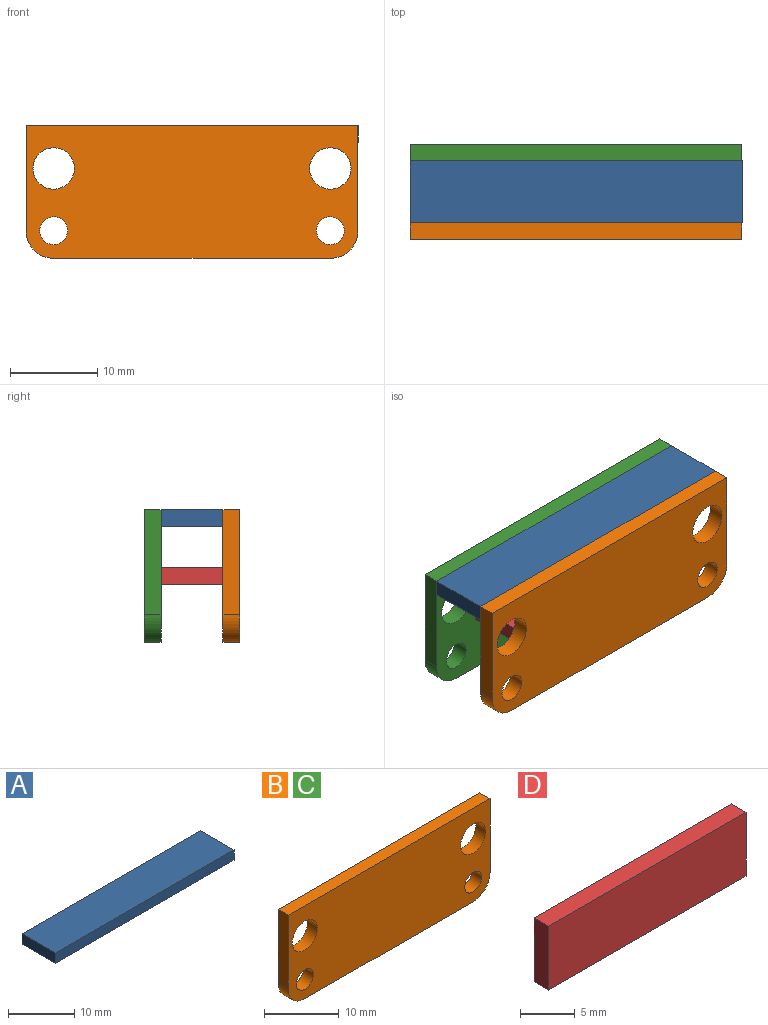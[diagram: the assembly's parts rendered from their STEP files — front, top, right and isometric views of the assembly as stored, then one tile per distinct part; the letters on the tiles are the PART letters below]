
ASSEMBLY  parts=4 mates=3
PART A: 6 faces, bbox 38.1x7.1x1.9 mm
  f0: plane 7.11x1.9mm, normal (-1,0,0), area 13.5mm2, adj f1,f3,f4,f5
  f1: plane 38.1x1.9mm, normal (0,-1,0), area 72.3mm2, adj f0,f2,f4,f5
  f2: plane 7.11x1.9mm, normal (1,0,0), area 13.5mm2, adj f1,f3,f4,f5
  f3: plane 38.1x1.9mm, normal (0,1,0), area 72.3mm2, adj f0,f2,f4,f5
  f4: plane 38.1x7.11mm, normal (0,0,1), area 271mm2, adj f0,f1,f2,f3
  f5: plane 38.1x7.11mm, normal (0,0,-1), area 271mm2, adj f0,f1,f2,f3
PART B: 12 faces, bbox 38.1x1.9x15.2 mm
  f0: cylinder r=3.17mm len=3.18mm, axis (0,1,0), area 9.5mm2, adj f1,f5,f10,f11
  f1: plane 12.05x1.9mm, normal (1,0,0), area 22.9mm2, adj f0,f2,f10,f11
  f2: plane 38.1x1.9mm, normal (0,0,1), area 72.3mm2, adj f1,f3,f10,f11
  f3: plane 12.05x1.9mm, normal (-1,0,0), area 22.9mm2, adj f2,f4,f10,f11
  f4: cylinder r=3.17mm len=3.18mm, axis (0,1,0), area 9.5mm2, adj f3,f5,f10,f11
  f5: plane 31.75x1.9mm, normal (0,0,-1), area 60.2mm2, adj f0,f4,f10,f11
  f6: cylinder r=2.38mm len=4.75mm, axis (0,1,0), area 28.3mm2, adj f10,f11
  f7: cylinder r=1.6mm len=3.2mm, axis (0,1,0), area 19.1mm2, adj f10,f11
  f8: cylinder r=2.38mm len=4.75mm, axis (0,1,0), area 28.3mm2, adj f10,f11
  f9: cylinder r=1.6mm len=3.2mm, axis (0,1,0), area 19.1mm2, adj f10,f11
  f10: plane 38.1x15.23mm, normal (0,-1,0), area 524.3mm2, adj f0,f1,f2,f3,f4,f5,f6,f7
  f11: plane 38.1x15.23mm, normal (0,1,0), area 524.3mm2, adj f0,f1,f2,f3,f4,f5,f6,f7
PART C: same geometry as B
PART D: 6 faces, bbox 25.4x1.9x7.1 mm
  f0: plane 7.11x1.9mm, normal (-1,0,0), area 13.5mm2, adj f1,f3,f4,f5
  f1: plane 25.4x1.9mm, normal (0,0,-1), area 48.2mm2, adj f0,f2,f4,f5
  f2: plane 7.11x1.9mm, normal (1,0,0), area 13.5mm2, adj f1,f3,f4,f5
  f3: plane 25.4x1.9mm, normal (0,0,1), area 48.2mm2, adj f0,f2,f4,f5
  f4: plane 25.4x7.11mm, normal (0,-1,0), area 180.6mm2, adj f0,f1,f2,f3
  f5: plane 25.4x7.11mm, normal (0,1,0), area 180.6mm2, adj f0,f1,f2,f3
PLACE A t=(-7.29,-8.88,10.41)mm
PLACE B t=(-16.64,1.2,-15.07)mm
PLACE C t=(-16.64,10.21,-15.07)mm
PLACE D rot(axis=(1,0,0),90deg) t=(7.81,22.26,5.66)mm
MATE fastened D.f3 <-> B.f11  axis (0,-1,0) through (-4.89,1.2,4.71)mm
MATE fastened B.f11 <-> A.f1  axis (0,1,0) through (-4.89,1.2,12.31)mm
MATE fastened C.f10 <-> A.f3  axis (0,-1,0) through (-4.89,8.31,12.31)mm
